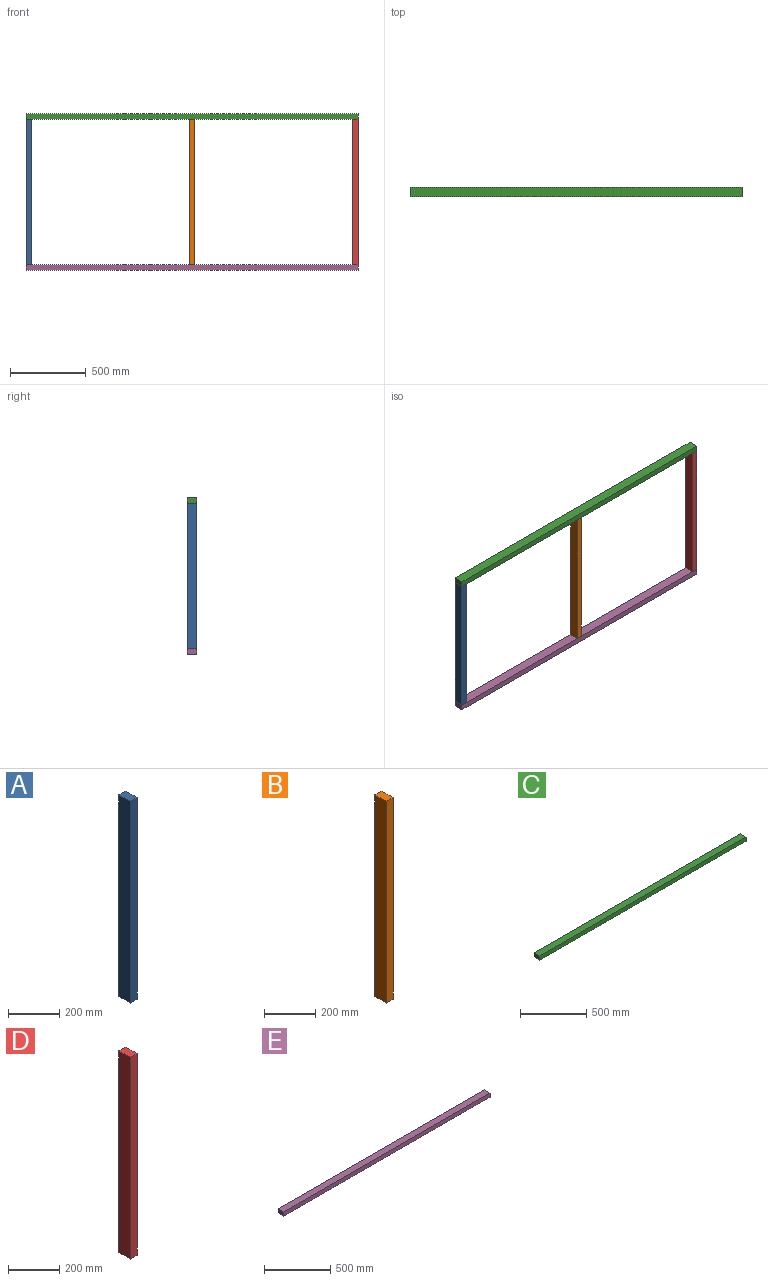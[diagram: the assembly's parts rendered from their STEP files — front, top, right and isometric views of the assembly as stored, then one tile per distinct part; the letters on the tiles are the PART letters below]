
ASSEMBLY  parts=5 mates=4
PART A: 6 faces, bbox 38x63x960 mm
  f0: plane 960x38mm, normal (0,-1,0), area 36480mm2, adj f1,f3,f4,f5
  f1: plane 960x63mm, normal (1,0,0), area 60480mm2, adj f0,f2,f4,f5
  f2: plane 960x38mm, normal (0,1,0), area 36480mm2, adj f1,f3,f4,f5
  f3: plane 960x63mm, normal (-1,0,0), area 60480mm2, adj f0,f2,f4,f5
  f4: plane 63x38mm, normal (0,0,1), area 2394mm2, adj f0,f1,f2,f3
  f5: plane 63x38mm, normal (0,0,-1), area 2394mm2, adj f0,f1,f2,f3
PART B: 6 faces, bbox 38x63x960 mm
  f0: plane 960x63mm, normal (1,0,0), area 60480mm2, adj f1,f3,f4,f5
  f1: plane 960x38mm, normal (0,1,0), area 36480mm2, adj f0,f2,f4,f5
  f2: plane 960x63mm, normal (-1,0,0), area 60480mm2, adj f1,f3,f4,f5
  f3: plane 960x38mm, normal (0,-1,0), area 36480mm2, adj f0,f2,f4,f5
  f4: plane 63x38mm, normal (0,0,1), area 2394mm2, adj f0,f1,f2,f3
  f5: plane 63x38mm, normal (0,0,-1), area 2394mm2, adj f0,f1,f2,f3
PART C: 6 faces, bbox 2195x63x38 mm
  f0: plane 63x38mm, normal (1,0,0), area 2394mm2, adj f1,f3,f4,f5
  f1: plane 2195x38mm, normal (0,1,0), area 83410mm2, adj f0,f2,f4,f5
  f2: plane 63x38mm, normal (-1,0,0), area 2394mm2, adj f1,f3,f4,f5
  f3: plane 2195x38mm, normal (0,-1,0), area 83410mm2, adj f0,f2,f4,f5
  f4: plane 2195x63mm, normal (0,0,-1), area 138285mm2, adj f0,f1,f2,f3
  f5: plane 2195x63mm, normal (0,0,1), area 138285mm2, adj f0,f1,f2,f3
PART D: 6 faces, bbox 38x63x960 mm
  f0: plane 960x38mm, normal (0,-1,0), area 36480mm2, adj f1,f3,f4,f5
  f1: plane 960x63mm, normal (1,0,0), area 60480mm2, adj f0,f2,f4,f5
  f2: plane 960x38mm, normal (0,1,0), area 36480mm2, adj f1,f3,f4,f5
  f3: plane 960x63mm, normal (-1,0,0), area 60480mm2, adj f0,f2,f4,f5
  f4: plane 63x38mm, normal (0,0,1), area 2394mm2, adj f0,f1,f2,f3
  f5: plane 63x38mm, normal (0,0,-1), area 2394mm2, adj f0,f1,f2,f3
PART E: 6 faces, bbox 2195x63x38 mm
  f0: plane 63x38mm, normal (1,0,0), area 2394mm2, adj f1,f3,f4,f5
  f1: plane 2195x38mm, normal (0,1,0), area 83410mm2, adj f0,f2,f4,f5
  f2: plane 63x38mm, normal (-1,0,0), area 2394mm2, adj f1,f3,f4,f5
  f3: plane 2195x38mm, normal (0,-1,0), area 83410mm2, adj f0,f2,f4,f5
  f4: plane 2195x63mm, normal (0,0,1), area 138285mm2, adj f0,f1,f2,f3
  f5: plane 2195x63mm, normal (0,0,-1), area 138285mm2, adj f0,f1,f2,f3
PLACE A t=(117.69,-1669.56,-649.85)mm
PLACE B t=(117.69,-1669.56,-649.85)mm
PLACE C t=(117.69,-1669.56,-649.85)mm
PLACE D t=(117.69,-1669.56,-649.85)mm
PLACE E t=(117.69,-1669.56,-649.85)mm
MATE fastened E.f3 <-> D.f0  axis (0,-1,0) through (92.58,-366.92,-611.85)mm
MATE fastened C.f3 <-> A.f0  axis (0,-1,0) through (-2102.42,-366.92,348.15)mm
MATE fastened C.f3 <-> D.f0  axis (0,-1,0) through (92.58,-366.92,348.15)mm
MATE fastened B.f3 <-> C.f3  axis (0,-1,0) through (-1004.92,-366.92,348.15)mm
